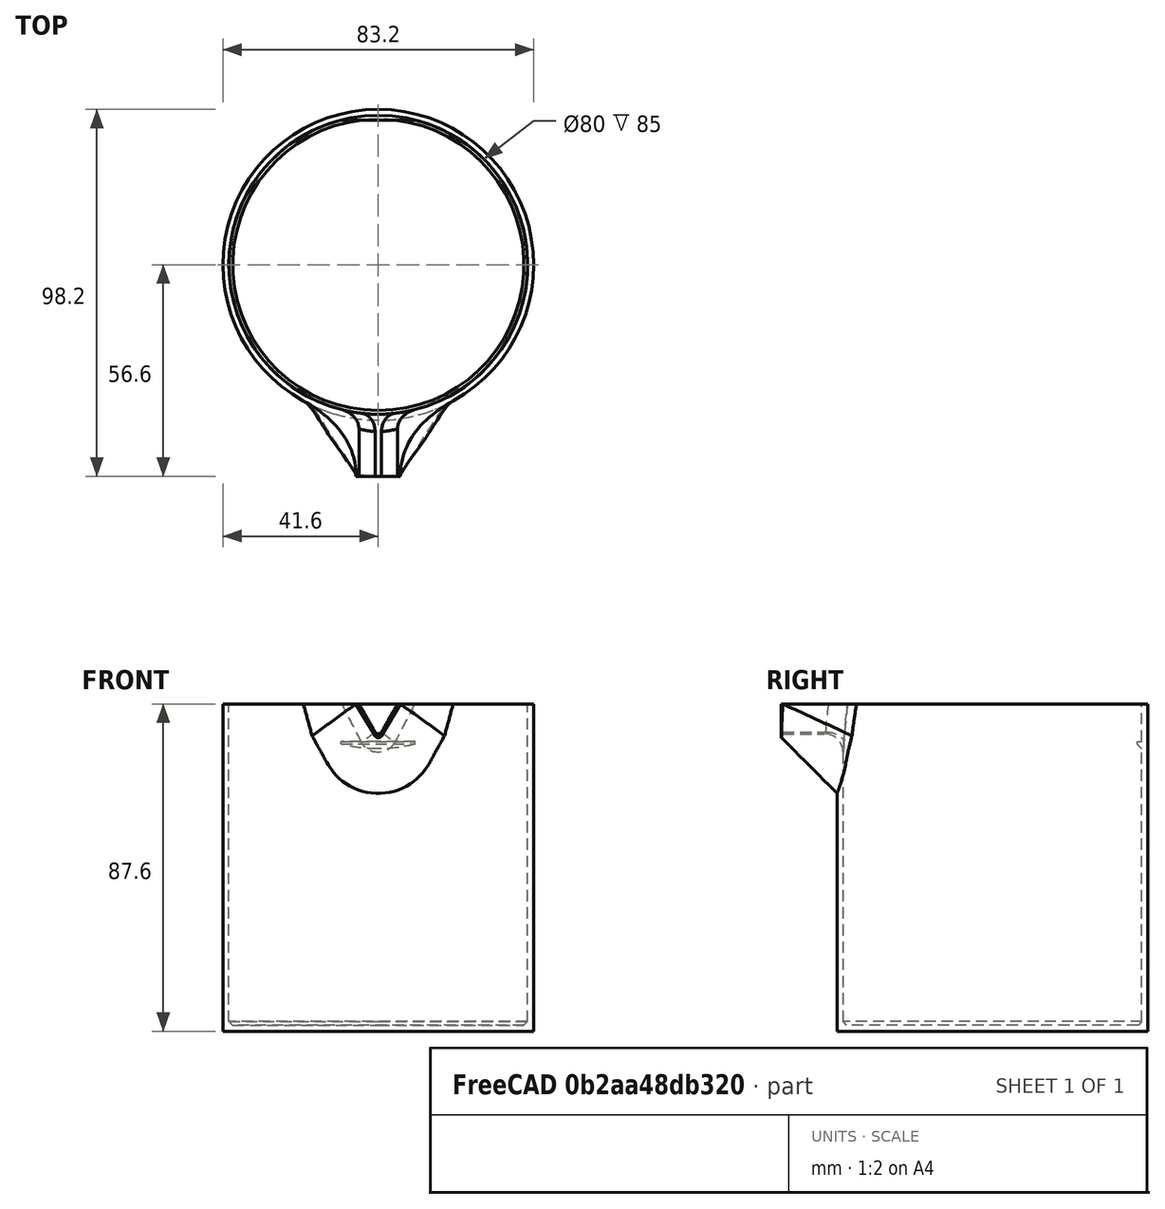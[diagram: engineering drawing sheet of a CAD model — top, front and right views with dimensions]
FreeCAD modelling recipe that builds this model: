
FCSTD DOCUMENT  (FreeCAD 1.1R44227 +647 (Git))
Label: Мерка
License: All rights reserved
LicenseURL: https://en.wikipedia.org/wiki/All_rights_reserved
objects: Sketcher::SketchObject×4, PartDesign::Fillet×3, PartDesign::Pad×2, PartDesign::Chamfer×2, App::Point×1, PartDesign::Revolution×1, PartDesign::Pocket×1, Part::DatumPlane×1, PartDesign::Body×1
note: 36 computed .brp shape members not serialized (recipe doc carries the construction recipe); baked Part::Feature solids carry a one-line shape summary decoded from their .brp

FEATURE [App::Point] Origin001
  Role = Origin
FEATURE [Sketcher::SketchObject] Sketch
  ArcFitTolerance = 1e-06
  AttachmentSupport = -> [Origin]
  ExternalTypes = [0]
  FullyConstrained = true
  MakeInternals = false
  MapMode = 5
  Placement = pos=(0,0,0) rot=(0.57735,0.57735,0.57735;2.0944rad)
  _ExternalGeoVersion = 1
  sketch-geometry (7):
    g0: LineSegment StartX=0 StartY=1.6 StartZ=0 EndX=40 EndY=1.6 EndZ=0
    g1: LineSegment StartX=40 StartY=1.6 StartZ=0 EndX=40 EndY=87.6 EndZ=0
    g2: LineSegment StartX=0 StartY=1.6 StartZ=0 EndX=0 EndY=0 EndZ=0
    g3: LineSegment StartX=41.6 StartY=1.6 StartZ=0 EndX=41.6 EndY=87.6 EndZ=0
    g4: LineSegment StartX=41.6 StartY=87.6 StartZ=0 EndX=40 EndY=87.6 EndZ=0
    g5: LineSegment StartX=0 StartY=0 StartZ=0 EndX=41.6 EndY=0 EndZ=0
    g6: LineSegment StartX=41.6 StartY=0 StartZ=0 EndX=41.6 EndY=1.6 EndZ=0
  constraints (20):
    c: Horizontal(g0)
    c: Vertical(g1)
    c: PointOnObject(g0,g-2)
    c: DistanceX(g0,g1) = 40
    c: DistanceY(g0,g1) = 86
    c: Coincident(g2,g0)
    c: Coincident(g2,g-1)
    c: DistanceY(g2,g2) = 1.6
    c: Vertical(g3)
    c: Horizontal(g1,g3)
    c: DistanceX(g1,g3) = 1.6
    c: Horizontal(g3,g1)
    c: Coincident(g4,g3)
    c: Coincident(g4,g1)
    c: Coincident(g0,g1)
    c: Coincident(g2,g5)
    c: Horizontal(g5)
    c: Coincident(g5,g6)
    c: Coincident(g6,g3)
    c: Vertical(g6)
FEATURE [PartDesign::Revolution] Revolution
  Angle = 360
  Angle2 = 0
  Axis = (0,0,1)
  Base = (0,0,0)
  FuseOrder = 0
  Profile = -> Sketch
  ReferenceAxis = -> Sketch [V_Axis]
  Refine = true
  Reversed = true
  Suppressed = false
  Type = 0
FEATURE [Sketcher::SketchObject] Sketch001
  ArcFitTolerance = 1e-06
  AttachmentSupport = -> [Origin]
  ExternalGeometry = -> [Revolution]
  ExternalTypes = [0,0]
  FullyConstrained = true
  MakeInternals = false
  MapMode = 5
  Placement = pos=(0,0,0) rot=(0.57735,0.57735,0.57735;2.0944rad)
  _ExternalGeoVersion = 1
  sketch-geometry (5):
    g0: LineSegment [constr] StartX=40 StartY=1.6 StartZ=0 EndX=40 EndY=77.6 EndZ=0
    g1: LineSegment StartX=38.75 StartY=76.85 StartZ=0 EndX=40 EndY=75.6 EndZ=0
    g2: LineSegment StartX=40 StartY=75.6 StartZ=0 EndX=40 EndY=77.6 EndZ=0
    g3: LineSegment StartX=40 StartY=77.6 StartZ=0 EndX=38.75 EndY=77.6 EndZ=0
    g4: LineSegment StartX=38.75 StartY=76.85 StartZ=0 EndX=38.75 EndY=77.6 EndZ=0
  constraints (14):
    c: DistanceY(g0,g0) = 76
    c: Coincident(g1,g2)
    c: Coincident(g2,g3)
    c: Vertical(g2)
    c: Angle(g2,g1) = 0.785398
    c: DistanceY(g1,g2) = 2
    c: PointOnObject(g2,g-3)
    c: Coincident(g0,g-3)
    c: Coincident(g4,g3)
    c: Vertical(g4)
    c: Coincident(g2,g0)
    c: Horizontal(g3)
    c: Coincident(g4,g1)
    c: DistanceX(g3,g3) = 1.25
FEATURE [PartDesign::Pad] Pad
  BaseFeature = -> Revolution
  Direction = (1,0,0)
  Length = 21.4
  Length2 = 10
  Profile = -> Sketch001
  ReferenceAxis = -> Sketch001 [N_Axis]
  Refine = true
  SideType = 2
  Suppressed = false
  Type = 0
  Type2 = 0
FEATURE [Sketcher::SketchObject] Sketch002
  ArcFitTolerance = 1e-06
  AttachmentSupport = -> [Origin]
  ExternalGeometry = -> [Pad]
  ExternalTypes = [0]
  FullyConstrained = true
  MakeInternals = false
  MapMode = 5
  Placement = pos=(0,0,0) rot=(1,0,0;1.5708rad)
  _ExternalGeoVersion = 1
  sketch-geometry (3):
    g0: LineSegment StartX=-3.5 StartY=87.6 StartZ=0 EndX=2.44e-14 EndY=81.5378 EndZ=0
    g1: LineSegment StartX=2.4e-14 StartY=81.5378 StartZ=0 EndX=3.5 EndY=87.6 EndZ=0
    g2: LineSegment StartX=3.5 StartY=87.6 StartZ=0 EndX=-3.5 EndY=87.6 EndZ=0
  constraints (8):
    c: Coincident(g0,g1)
    c: Coincident(g1,g2)
    c: Coincident(g2,g0)
    c: Equal(g2,g0)
    c: DistanceX(g2,g2) = 7
    c: Equal(g1,g0)
    c: Symmetric(g1,g0,g-2)
    c: PointOnObject(g1,g-3)
FEATURE [PartDesign::Pocket] Pocket
  BaseFeature = -> Pad
  Direction = (0,1,-2e-16)
  Length = 5
  Length2 = 5
  Profile = -> Sketch002
  ReferenceAxis = -> Sketch002 [N_Axis]
  Refine = true
  Reversed = true
  SideType = 0
  Suppressed = false
  TaperAngle = 2
  Type = 1
  Type2 = 0
FEATURE [Part::DatumPlane] DatumPlane
  AttachmentSupport = -> [Pocket]
  MapMode = 6
  Placement = pos=(4.2e-14,-41.6,78.6324) rot=(0,0.707107,-0.707107;3.14159rad)
FEATURE [Sketcher::SketchObject] Sketch003
  ArcFitTolerance = 1e-06
  AttachmentSupport = -> [DatumPlane]
  ExternalGeometry = -> [Pocket]
  ExternalTypes = [0,0]
  FullyConstrained = true
  MakeInternals = false
  MapMode = 5
  Placement = pos=(4.2e-14,-41.6,78.6324) rot=(0,0.707107,-0.707107;3.14159rad)
  _ExternalGeoVersion = 1
  sketch-geometry (4):
    g0: LineSegment StartX=-5.16446 StartY=-8.96759 StartZ=0 EndX=-5.96446 EndY=-8.96759 EndZ=0
    g1: LineSegment StartX=-5.96446 StartY=-8.96759 StartZ=0 EndX=0 EndY=1 EndZ=0
    g2: LineSegment StartX=0 StartY=1 StartZ=0 EndX=5.96446 EndY=-8.96759 EndZ=0
    g3: LineSegment StartX=5.96446 StartY=-8.96759 StartZ=0 EndX=5.16446 EndY=-8.96759 EndZ=0
  constraints (11):
    c: Coincident(g0,g-3)
    c: Horizontal(g0)
    c: Coincident(g0,g1)
    c: PointOnObject(g1,g-2)
    c: Coincident(g1,g2)
    c: Coincident(g2,g3)
    c: Coincident(g3,g-4)
    c: Horizontal(g3)
    c: Equal(g2,g1)
    c: Distance(g-4,g1) = 1
    c: DistanceX(g3,g3) = 0.8
FEATURE [PartDesign::Pad] Pad001
  BaseFeature = -> Pocket
  Direction = (1e-15,-1,-2e-16)
  Length = 15
  Length2 = 1
  Profile = -> Sketch003
  ReferenceAxis = -> Sketch003 [N_Axis]
  Refine = true
  SideType = 1
  Suppressed = false
  Type = 0
  Type2 = 0
FEATURE [PartDesign::Fillet] Fillet
  Base = -> Pad001 [Edge18,Edge8]
  BaseFeature = -> Pad001
  Radius = 1
  Refine = true
  SupportTransform = false
  Suppressed = false
  UseAllEdges = false
FEATURE [PartDesign::Fillet] Fillet001
  Base = -> Fillet [Edge26]
  BaseFeature = -> Fillet
  Radius = 5
  Refine = true
  SupportTransform = false
  Suppressed = false
  UseAllEdges = false
FEATURE [PartDesign::Fillet] Fillet002
  Base = -> Fillet001 [Edge35]
  BaseFeature = -> Fillet001
  Radius = 0.5
  Refine = true
  SupportTransform = false
  Suppressed = false
  UseAllEdges = false
FEATURE [PartDesign::Chamfer] Chamfer
  Angle = 45
  Base = -> Fillet002 [Edge39]
  BaseFeature = -> Fillet002
  ChamferType = 0
  FlipDirection = false
  Refine = true
  Size = 14.9
  Size2 = 1
  SupportTransform = false
  Suppressed = false
  UseAllEdges = false
FEATURE [PartDesign::Chamfer] Chamfer001
  Angle = 45
  Base = -> Chamfer [Edge50]
  BaseFeature = -> Chamfer
  ChamferType = 0
  FlipDirection = false
  Refine = true
  Size = 1
  Size2 = 1
  SupportTransform = false
  Suppressed = false
  UseAllEdges = false
FEATURE [PartDesign::Body] Body
  AllowCompound = true
  Group = -> [Sketch,Revolution,Sketch001,Pad,Sketch002,Pocket,DatumPlane,Sketch003,Pad001,Fillet,Fillet001,Fillet002,Chamfer,Chamfer001]
  Origin = -> Origin
  Tip = -> Chamfer001
